# Revit family: Sink-Wall_Mount-Utility-KOHLER-Gilford-K-12784_1
name_source: partatom
category: Plumbing Fixtures
revit_build: Autodesk Revit 2015 (Build: 20140606_1530(x64)
units: mm (PartAtom-declared; Revit-internal decimal feet)

## types (1)
- 0-White
    ADA Compliant = No
    Assembly Code = D2010400
    CW Connection = No
    Cold Water Inlet = Cold Water Inlet
    Date Modified = 09/09/2019
    Default Elevation = 36"
    Description = 24 Inch x 22 Inch bracket-mounted scrub-up/plaster sink with single faucet hole
    Drain Included = No
    Finish = Kohler-Vitreous_China-0-White
    HW Connection = No
    Height = 17 1/2"
    Hot Water Inlet = Hot Water Inlet
    Length = 22 1/8"
    Manufacturer = KOHLER Co.
    MasterFormat 1995 = 15410
    MasterFormat 2004 = 22.41.16
    Material = Vitreous China
    Model = K-12784-0
    Product Documentation Link = https://www.us.kohler.com
    Product Name = Gilford
    Product Page URL = http://www.us.kohler.com
    URL = https://www.us.kohler.com
    Vent Connection = No
    Waste Connection = Yes
    Waste Water Outlet = Waste Water Outlet
    WaterSense Certified = No
    Width = 24"

## geometry (parser evidence)
native form markers: Sweep x3
no freeform markers — native parametric forms only
